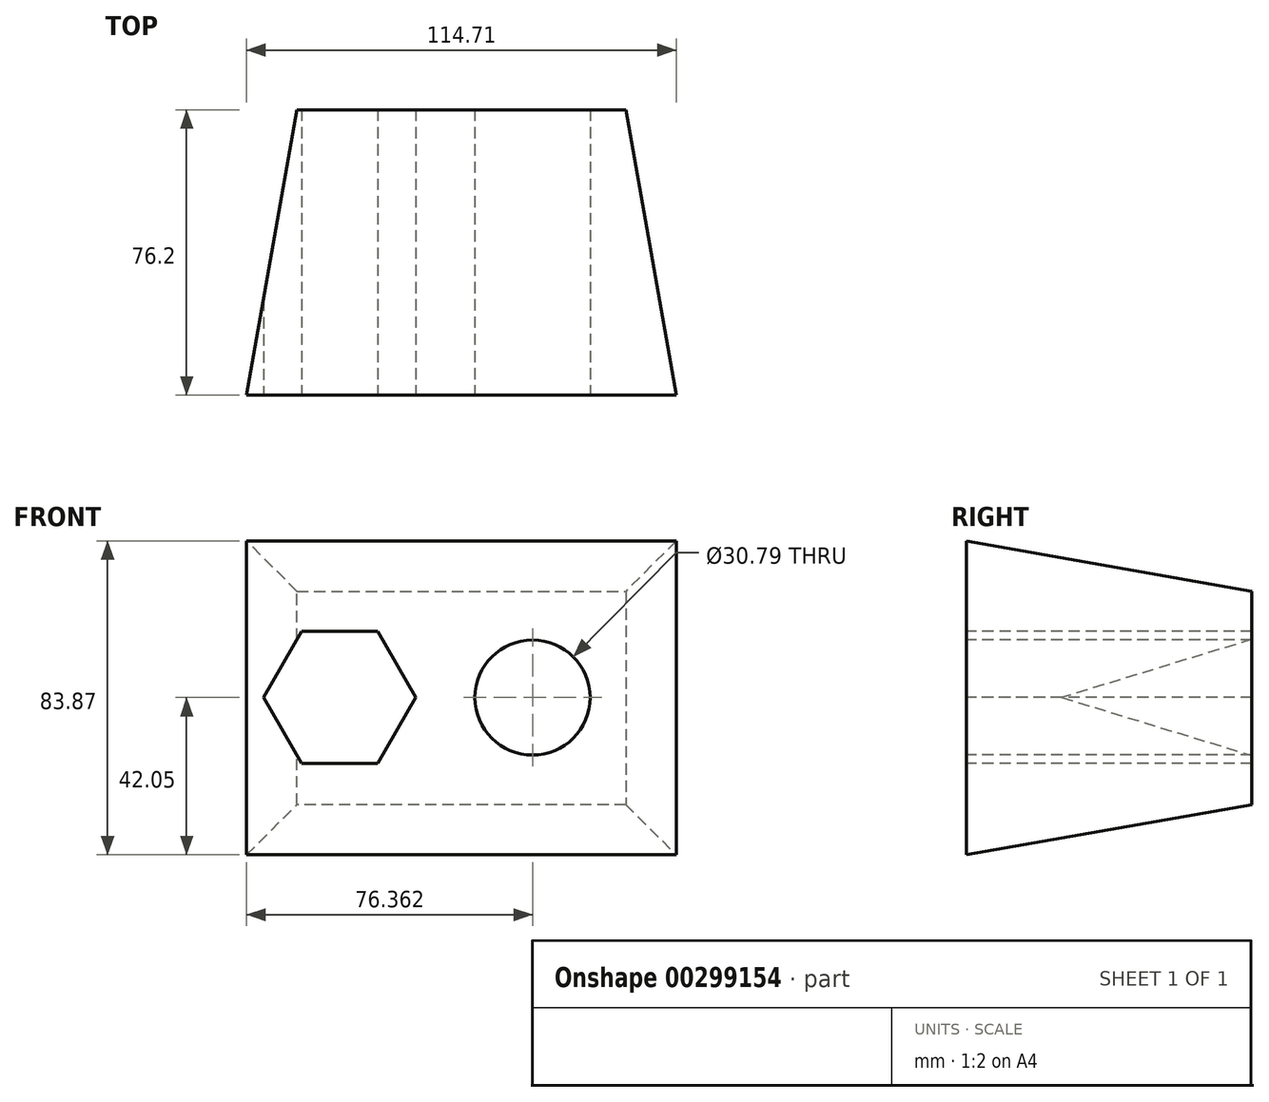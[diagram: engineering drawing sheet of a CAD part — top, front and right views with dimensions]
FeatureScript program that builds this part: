
annotation { "Feature Type Name" : "Feature", "Feature Type Description" : "" }
export const myFeature = defineFeature(function(context is Context, id is Id, definition is map)
    precondition{}
    {
        {
            var Q0;
            Q0=qCreatedBy(makeId("Front.planeOp"),FACE);
            var sketch = newSketch(context, id + "F0", { "sketchPlane" : qUnion([Q0])});
            skLineSegment(sketch, "E0.bottom", {"start": v(-41.82, 28.38) * mm, "end": v(46.02, 28.38) * mm});
            skLineSegment(sketch, "E0.top", {"start": v(-41.82, -28.62) * mm, "end": v(46.02, -28.62) * mm});
            skLineSegment(sketch, "E0.left", {"start": v(-41.82, 28.38) * mm, "end": v(-41.82, -28.62) * mm});
            skLineSegment(sketch, "E0.right", {"start": v(46.02, 28.38) * mm, "end": v(46.02, -28.62) * mm});
            skSolve(sketch);
        }
        {
            var Q0;
            Q0=makeQuery(id+"F0.imprint","IMPRINT",FACE,{"disambiguationData":[TD([[makeQuery(id+"F0.imprint","IMPRINT",EDGE,{"derivedFrom":sQuery(id+"F0.wireOp",EDGE,"E0.bottom")}),-1.0]])]});
            extrude(context, id + "F1", {"entities" : qUnion([Q0]), "depth" : 76.2 * mm, "hasDraft" : true, "draftAngle" : 10 * degree});
        }
        {
            var Q0;
            Q0=makeQuery(id+"F1.opExtrude","CAP_FACE",FACE,{"disambiguationData":[OSD([sQuery(id+"F0.wireOp",EDGE,"E0.bottom"),sQuery(id+"F0.wireOp",EDGE,"E0.top"),sQuery(id+"F0.wireOp",EDGE,"E0.left"),sQuery(id+"F0.wireOp",EDGE,"E0.right")])],"isStart":false});
            var sketch = newSketch(context, id + "F2", { "sketchPlane" : qUnion([Q0])});
            skCircle(sketch, "E1", {"center": v(21.11, 0) * mm, "radius": 15.4 * mm});
            skCircle(sketch, "E2.cCircle", {"center": v(-30.4, 0) * mm, "radius": 17.64 * mm, "construction": true});
            skLineSegment(sketch, "E2.0", {"start": v(-20.22, -17.64) * mm, "end": v(-40.59, -17.64) * mm});
            skLineSegment(sketch, "E2.1", {"start": v(-40.59, -17.64) * mm, "end": v(-50.77, 0) * mm});
            skLineSegment(sketch, "E2.2", {"start": v(-50.77, 0) * mm, "end": v(-40.59, 17.64) * mm});
            skLineSegment(sketch, "E2.3", {"start": v(-40.59, 17.64) * mm, "end": v(-20.22, 17.64) * mm});
            skLineSegment(sketch, "E2.4", {"start": v(-20.22, 17.64) * mm, "end": v(-10.03, 0) * mm});
            skLineSegment(sketch, "E2.5", {"start": v(-10.03, 0) * mm, "end": v(-20.22, -17.64) * mm});
            skPoint(sketch, "E2.0.midPoint", {"position": v(-30.4, -17.64) * mm});
            skSolve(sketch);
        }
        {
            var Q0;
            Q0 = qSketchRegion(id + "F2", true);
            extrude(context, id + "F3", {"entities" : qUnion([Q0]), "operationType" : NewBodyOperationType.REMOVE, "endBound" : BoundingType.THROUGH_ALL, "oppositeDirection" : true, "depth" : 25.4 * mm});
        }
    });
